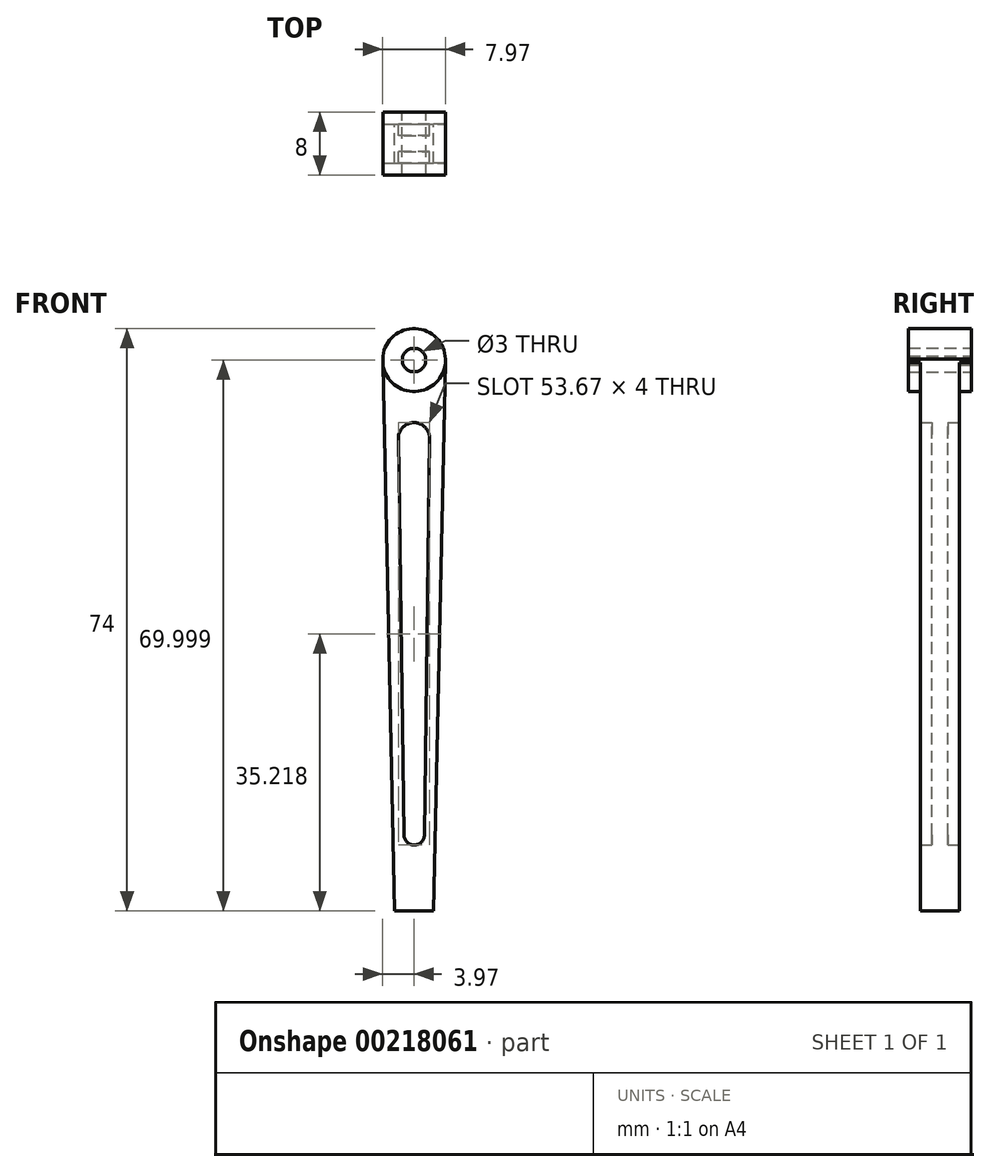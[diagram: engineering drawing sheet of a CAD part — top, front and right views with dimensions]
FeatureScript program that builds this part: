
annotation { "Feature Type Name" : "Feature", "Feature Type Description" : "" }
export const myFeature = defineFeature(function(context is Context, id is Id, definition is map)
    precondition{}
    {
        {
            var Q0;
            Q0=qCreatedBy(makeId("Front.planeOp"),FACE);
            var sketch = newSketch(context, id + "F0", { "sketchPlane" : qUnion([Q0])});
            skLineSegment(sketch, "E0", {"start": v(-2.5, -45.4) * mm, "end": v(2.5, -45.4) * mm});
            skCircle(sketch, "E1", {"center": v(0, 24.6) * mm, "radius": 1.5 * mm});
            skCircle(sketch, "E2", {"center": v(0, 24.6) * mm, "radius": 4 * mm});
            skLineSegment(sketch, "E3", {"start": v(-3.97, 25.1) * mm, "end": v(-2.5, -45.4) * mm});
            skLineSegment(sketch, "E4", {"start": v(4, 24.74) * mm, "end": v(2.5, -45.4) * mm});
            skArc(sketch, "E5", {"start": v(2, 14.64) * mm, "mid": v(0, 16.66) * mm, "end": v(-2, 14.63) * mm});
            skArc(sketch, "E6", {"start": v(-1.27, -35.73) * mm, "mid": v(0.02, -37) * mm, "end": v(1.32, -35.73) * mm});
            skLineSegment(sketch, "E7", {"start": v(-1.27, -35.73) * mm, "end": v(-2, 14.63) * mm});
            skLineSegment(sketch, "E8.MirrorCS", {"start": v(1.32, -35.73) * mm, "end": v(2, 14.64) * mm});
            skSolve(sketch);
        }
        {
            var Q0;
            Q0=makeQuery(id+"F0.imprint","IMPRINT",FACE,{"disambiguationData":[TD([[makeQuery(id+"F0.imprint","IMPRINT",EDGE,{"derivedFrom":sQuery(id+"F0.wireOp",EDGE,"Kk023S7X-x4Ik-aRJz-KUeV-EzDWMz7YOAeK.left")}),1.0]])]});
            var Q1;
            Q1=makeQuery(id+"F0.imprint","IMPRINT",FACE,{"disambiguationData":[TD([[makeQuery(id+"F0.imprint","IMPRINT",EDGE,{"derivedFrom":sQuery(id+"F0.wireOp",EDGE,"E0")}),1.0]])]});
            extrude(context, id + "F1", {"entities" : qUnion([Q0, Q1]), "endBound" : BoundingType.SYMMETRIC, "depth" : 5 * mm});
        }
        {
            var Q0;
            Q0=makeQuery(id+"F0.imprint","IMPRINT",FACE,{"disambiguationData":[TD([[makeQuery(id+"F0.imprint","IMPRINT",EDGE,{"derivedFrom":sQuery(id+"F0.wireOp",EDGE,"E1")}),-1.0]])]});
            extrude(context, id + "F2", {"entities" : qUnion([Q0]), "operationType" : NewBodyOperationType.ADD, "endBound" : BoundingType.SYMMETRIC, "depth" : 8 * mm});
        }
        {
            var Q0;
            Q0=makeQuery(id+"F0.imprint","IMPRINT",FACE,{"disambiguationData":[TD([[makeQuery(id+"F0.imprint","IMPRINT",EDGE,{"derivedFrom":sQuery(id+"F0.wireOp",EDGE,"E5")}),1.0]])]});
            extrude(context, id + "F3", {"entities" : qUnion([Q0]), "operationType" : NewBodyOperationType.ADD, "endBound" : BoundingType.SYMMETRIC, "depth" : 2 * mm});
        }
    });
